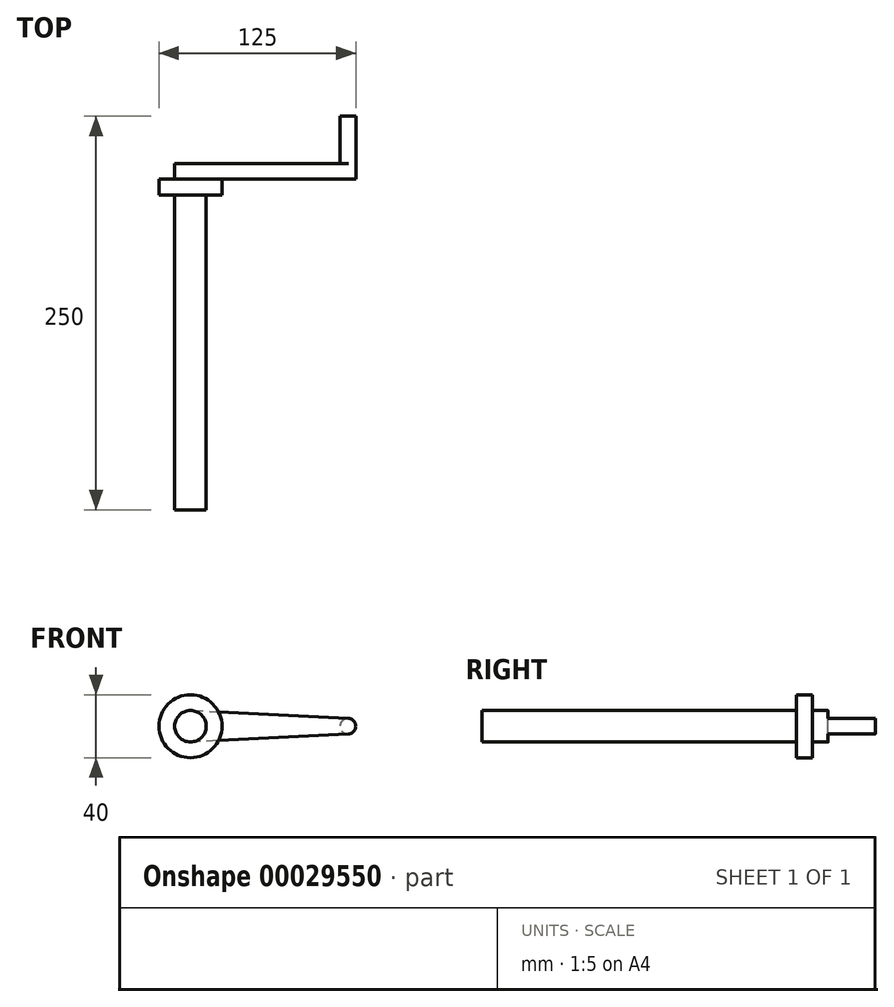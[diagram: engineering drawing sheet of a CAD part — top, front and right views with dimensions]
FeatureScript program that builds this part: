
annotation { "Feature Type Name" : "Feature", "Feature Type Description" : "" }
export const myFeature = defineFeature(function(context is Context, id is Id, definition is map)
    precondition{}
    {
        {
            var Q0;
            Q0=qCreatedBy(makeId("Front.planeOp"),FACE);
            var sketch = newSketch(context, id + "F0", { "sketchPlane" : qUnion([Q0])});
            skCircle(sketch, "E0", {"center": v(0, 0) * mm, "radius": 10 * mm});
            skSolve(sketch);
        }
        {
            var Q0;
            Q0=makeQuery(id+"F0.imprint","IMPRINT",FACE,{"disambiguationData":[TD([[makeQuery(id+"F0.imprint","IMPRINT",EDGE,{"derivedFrom":sQuery(id+"F0.wireOp",EDGE,"E0")}),1.0]])]});
            extrude(context, id + "F1", {"entities" : qUnion([Q0]), "depth" : 200 * mm});
        }
        {
            var Q0;
            Q0=qCreatedBy(makeId("Front.planeOp"),FACE);
            var sketch = newSketch(context, id + "F2", { "sketchPlane" : qUnion([Q0])});
            skCircle(sketch, "E1", {"center": v(0, 0) * mm, "radius": 20 * mm});
            skSolve(sketch);
        }
        {
            var Q0;
            Q0=makeQuery(id+"F2.imprint","IMPRINT",FACE,{"disambiguationData":[TD([[makeQuery(id+"F2.imprint","IMPRINT",EDGE,{"derivedFrom":sQuery(id+"F2.wireOp",EDGE,"E1")}),1.0]])]});
            extrude(context, id + "F3", {"entities" : qUnion([Q0]), "operationType" : NewBodyOperationType.ADD, "oppositeDirection" : true, "depth" : 10 * mm});
        }
        {
            var Q0;
            Q0=makeQuery(id+"F3.opExtrude","CAP_FACE",FACE,{"disambiguationData":[OSD([sQuery(id+"F2.wireOp",EDGE,"E1")])],"isStart":false});
            var sketch = newSketch(context, id + "F4", { "sketchPlane" : qUnion([Q0])});
            skArc(sketch, "E2", {"start": v(-0.5, -9.99) * mm, "mid": v(10, 0) * mm, "end": v(-0.5, 9.99) * mm});
            skArc(sketch, "E3", {"start": v(-100.25, 5) * mm, "mid": v(-105, 0) * mm, "end": v(-100.25, -5) * mm});
            skLineSegment(sketch, "E4", {"start": v(-0.5, 9.99) * mm, "end": v(-100.25, 5) * mm});
            skLineSegment(sketch, "E5", {"start": v(-100.25, -5) * mm, "end": v(-0.5, -9.99) * mm});
            skSolve(sketch);
        }
        {
            var Q0;
            {var subQ5=sQuery(id+"F4.wireOp",EDGE,"E2");Q0=makeQuery(id+"F4.imprint","IMPRINT",FACE,{"disambiguationData":[TD([[makeQuery(id+"F4.imprint","IMPRINT",EDGE,{"derivedFrom":subQ5}),1.0]])]});}
            var Q1;
            {var subQ5=sQuery(id+"F4.wireOp",EDGE,"E3");Q1=makeQuery(id+"F4.imprint","IMPRINT",FACE,{"disambiguationData":[TD([[makeQuery(id+"F4.imprint","IMPRINT",EDGE,{"derivedFrom":subQ5}),1.0]])]});}
            extrude(context, id + "F5", {"entities" : qUnion([Q0, Q1]), "operationType" : NewBodyOperationType.ADD, "depth" : 10 * mm});
        }
        {
            var Q0;
            Q0=makeQuery(id+"F5.opExtrude","CAP_FACE",FACE,{"disambiguationData":[OSD([sQuery(id+"F4.wireOp",EDGE,"E2"),sQuery(id+"F4.wireOp",EDGE,"E3"),sQuery(id+"F4.wireOp",EDGE,"E4"),sQuery(id+"F4.wireOp",EDGE,"E5")])],"isStart":false});
            var sketch = newSketch(context, id + "F6", { "sketchPlane" : qUnion([Q0])});
            skCircle(sketch, "E6", {"center": v(-100, 0) * mm, "radius": 5 * mm});
            skSolve(sketch);
        }
        {
            var Q0;
            {var subQ0=sQuery(id+"F6.wireOp",EDGE,"E6");var subQ2=makeQuery(id+"F6.imprint","INTERSECT",VERTEX,{"derivedFrom":[makeQuery(id+"F5.opExtrude","CAP_EDGE",EDGE,{"disambiguationData":[OSD([sQuery(id+"F4.wireOp",EDGE,"E4")])],"isStart":false}),subQ0]});Q0=makeQuery(id+"F6.imprint","IMPRINT",FACE,{"disambiguationData":[TD([[makeQuery(id+"F6.imprint","IMPRINT",EDGE,{"disambiguationData":[TD([[subQ2,-1.0]])],"derivedFrom":subQ0}),1.0]])]});}
            extrude(context, id + "F7", {"entities" : qUnion([Q0]), "operationType" : NewBodyOperationType.ADD, "depth" : 30 * mm});
        }
    });
